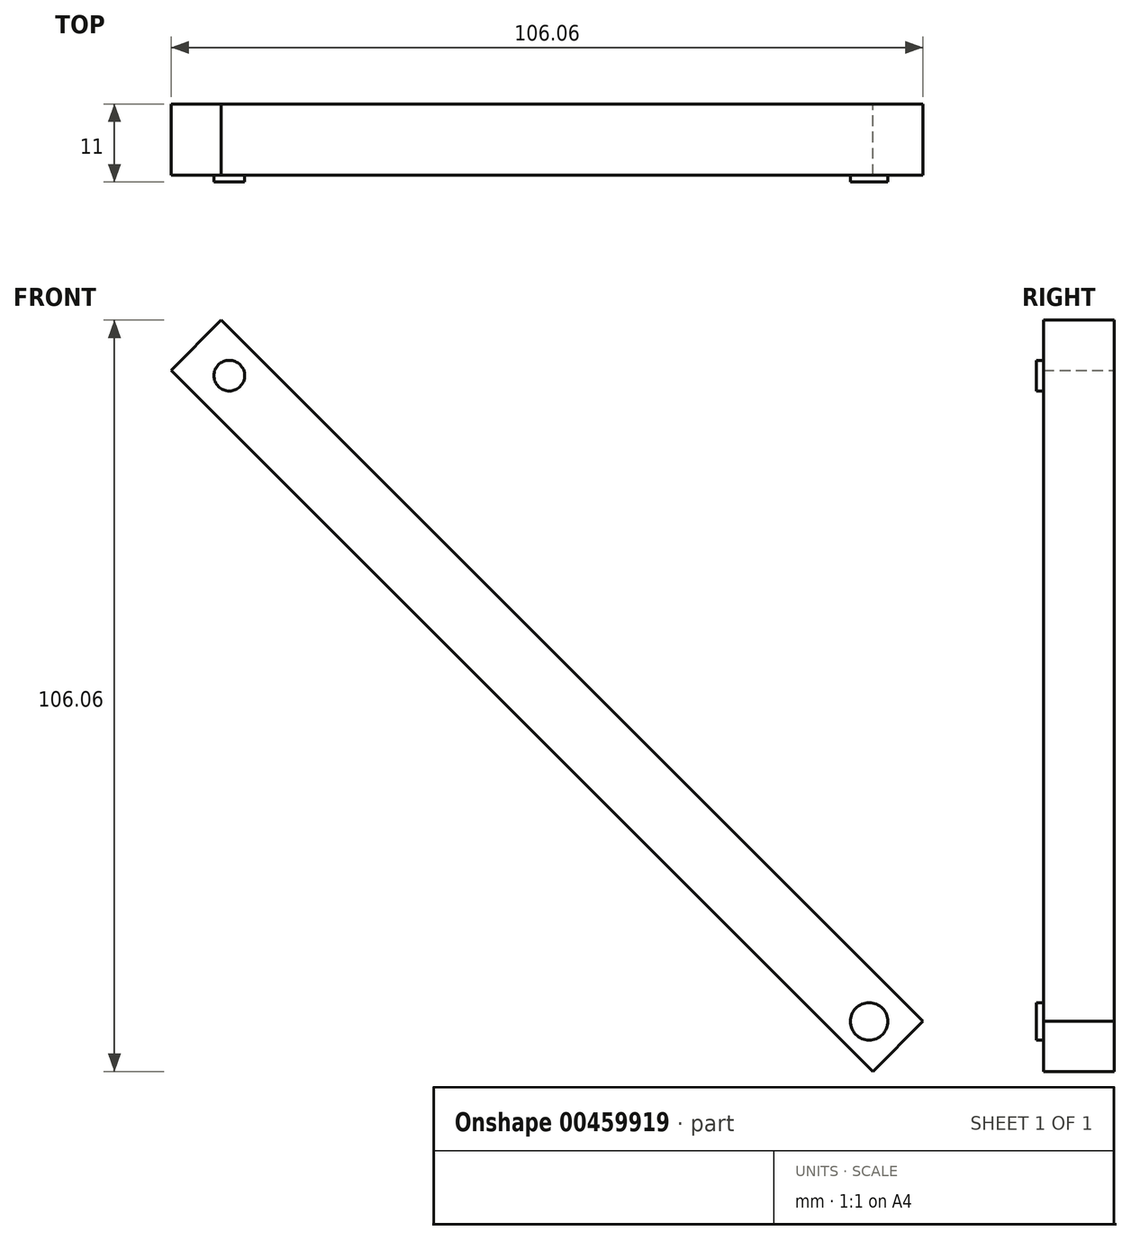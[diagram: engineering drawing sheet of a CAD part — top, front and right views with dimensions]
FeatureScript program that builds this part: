
annotation { "Feature Type Name" : "Feature", "Feature Type Description" : "" }
export const myFeature = defineFeature(function(context is Context, id is Id, definition is map)
    precondition{}
    {
        {
            var Q0;
            Q0=qCreatedBy(makeId("Front.planeOp"),FACE);
            var sketch = newSketch(context, id + "F0", { "sketchPlane" : qUnion([Q0])});
            skLineSegment(sketch, "E0", {"start": v(-56.55, 91.92) * mm, "end": v(42.44, -7.07) * mm});
            skLineSegment(sketch, "E1", {"start": v(42.44, -7.07) * mm, "end": v(-67.5, -7.07) * mm});
            skLineSegment(sketch, "E2", {"start": v(-56.55, 91.92) * mm, "end": v(-49.48, 99) * mm});
            skLineSegment(sketch, "E3", {"start": v(-49.48, 99) * mm, "end": v(49.51, 0) * mm});
            skLineSegment(sketch, "E4", {"start": v(49.51, 0) * mm, "end": v(42.44, -7.07) * mm});
            skSolve(sketch);
        }
        {
            var Q0;
            Q0=makeQuery(id+"F0.imprint","IMPRINT",FACE,{"disambiguationData":[TD([[makeQuery(id+"F0.imprint","IMPRINT",EDGE,{"derivedFrom":sQuery(id+"F0.wireOp",EDGE,"E0")}),1.0]])]});
            extrude(context, id + "F1", {"entities" : qUnion([Q0]), "depth" : 10 * mm});
        }
        {
            var Q0;
            Q0=makeQuery(id+"F1.opExtrude","CAP_FACE",FACE,{"disambiguationData":[OSD([sQuery(id+"F0.wireOp",EDGE,"E0"),sQuery(id+"F0.wireOp",EDGE,"E2"),sQuery(id+"F0.wireOp",EDGE,"E3"),sQuery(id+"F0.wireOp",EDGE,"E4")])],"isStart":false});
            var sketch = newSketch(context, id + "F2", { "sketchPlane" : qUnion([Q0])});
            skCircle(sketch, "E5", {"center": v(41.93, 0) * mm, "radius": 2.64 * mm});
            skCircle(sketch, "E6", {"center": v(-48.34, 91.16) * mm, "radius": 2.17 * mm});
            skSolve(sketch);
        }
        {
            var Q0;
            Q0=makeQuery(id+"F2.imprint","IMPRINT",FACE,{"disambiguationData":[TD([[makeQuery(id+"F2.imprint","IMPRINT",EDGE,{"derivedFrom":sQuery(id+"F2.wireOp",EDGE,"r5UgoJhh-mOlS-PHIk-XrEQ-OgkyjFRXeK5q")}),1.0]])]});
            var Q1;
            Q1=makeQuery(id+"F2.imprint","IMPRINT",FACE,{"disambiguationData":[TD([[makeQuery(id+"F2.imprint","IMPRINT",EDGE,{"derivedFrom":sQuery(id+"F2.wireOp",EDGE,"E5")}),1.0]])]});
            var Q2;
            Q2=makeQuery(id+"F2.imprint","IMPRINT",FACE,{"disambiguationData":[TD([[makeQuery(id+"F2.imprint","IMPRINT",EDGE,{"derivedFrom":sQuery(id+"F2.wireOp",EDGE,"E6")}),1.0]])]});
            extrude(context, id + "F3", {"entities" : qUnion([Q0, Q1, Q2]), "operationType" : NewBodyOperationType.ADD, "depth" : 1 * mm});
        }
    });
